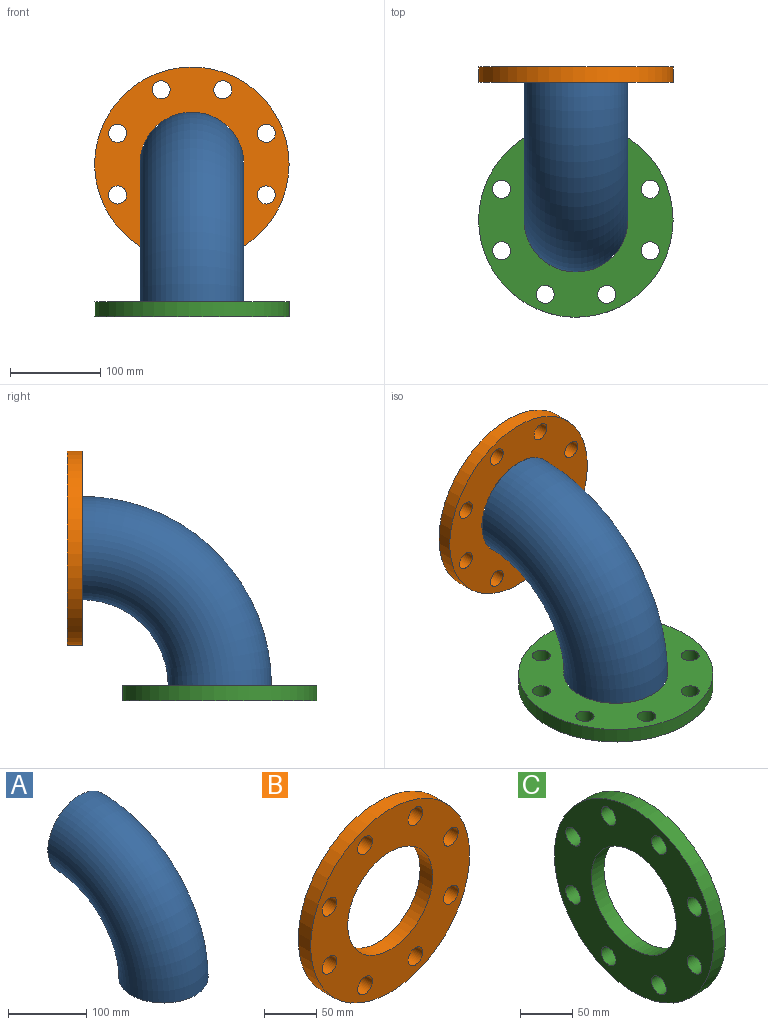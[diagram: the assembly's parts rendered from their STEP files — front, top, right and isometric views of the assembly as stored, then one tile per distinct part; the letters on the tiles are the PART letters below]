
ASSEMBLY  parts=3 mates=1
PART A: 4 faces, bbox 114.3x226.4x226.4 mm
  f0: plane 114.3x114.3mm, normal (0,0,-1), area 2041.4mm2, adj f2,f3
  f1: plane 114.3x114.3mm, normal (0,1,0), area 2041.4mm2, adj f2,f3
  f2: torus R=152mm, axis (-1,0,0), area 85735.3mm2, adj f0,f1
  f3: torus R=152mm, axis (-1,0,0), area 76734.2mm2, adj f0,f1
PART B: 12 faces, bbox 215x17x215 mm
  f0: cylinder r=57.5mm len=115mm, axis (0,-1,0), area 6141.8mm2, adj f10,f11
  f1: cylinder r=10mm len=20mm, axis (0,-1,0), area 1068.1mm2, adj f10,f11
  f2: cylinder r=10mm len=20mm, axis (0,-1,0), area 1068.1mm2, adj f10,f11
  f3: cylinder r=10mm len=20mm, axis (0,-1,0), area 1068.1mm2, adj f10,f11
  f4: cylinder r=10mm len=20mm, axis (0,-1,0), area 1068.1mm2, adj f10,f11
  f5: cylinder r=10mm len=20mm, axis (0,-1,0), area 1068.1mm2, adj f10,f11
  f6: cylinder r=10mm len=20mm, axis (0,-1,0), area 1068.1mm2, adj f10,f11
  f7: cylinder r=10mm len=20mm, axis (0,-1,0), area 1068.1mm2, adj f10,f11
  f8: cylinder r=10mm len=20mm, axis (0,-1,0), area 1068.1mm2, adj f10,f11
  f9: cylinder r=107.5mm len=215mm, axis (0,-1,0), area 11482.5mm2, adj f10,f11
  f10: plane 215x215mm, normal (0,1,0), area 23404.9mm2, adj f0,f1,f2,f3,f4,f5,f6,f7
  f11: plane 215x215mm, normal (0,-1,0), area 23404.9mm2, adj f0,f1,f2,f3,f4,f5,f6,f7
PART C: 12 faces, bbox 17x215x215 mm
  f0: cylinder r=57.5mm len=115mm, axis (1,0,0), area 6141.8mm2, adj f10,f11
  f1: cylinder r=10mm len=20mm, axis (1,0,0), area 1068.1mm2, adj f10,f11
  f2: cylinder r=10mm len=20mm, axis (1,0,0), area 1068.1mm2, adj f10,f11
  f3: cylinder r=10mm len=20mm, axis (1,0,0), area 1068.1mm2, adj f10,f11
  f4: cylinder r=10mm len=20mm, axis (1,0,0), area 1068.1mm2, adj f10,f11
  f5: cylinder r=10mm len=20mm, axis (1,0,0), area 1068.1mm2, adj f10,f11
  f6: cylinder r=10mm len=20mm, axis (1,0,0), area 1068.1mm2, adj f10,f11
  f7: cylinder r=10mm len=20mm, axis (1,0,0), area 1068.1mm2, adj f10,f11
  f8: cylinder r=10mm len=20mm, axis (1,0,0), area 1068.1mm2, adj f10,f11
  f9: cylinder r=107.5mm len=215mm, axis (1,0,0), area 11482.5mm2, adj f10,f11
  f10: plane 215x215mm, normal (-1,0,0), area 23404.9mm2, adj f0,f1,f2,f3,f4,f5,f6,f7
  f11: plane 215x215mm, normal (1,0,0), area 23404.9mm2, adj f0,f1,f2,f3,f4,f5,f6,f7
PLACE A t=(-126.16,61.92,-82.86)mm
PLACE B t=(-126.16,61.92,-82.86)mm fixed
PLACE C rot(axis=(0.58,0.58,-0.58),120deg) t=(25.84,61.92,-251.86)mm
MATE fastened C.f0 <-> A.f2  axis (0,0,-1) through (-126.16,-90.08,-99.86)mm
